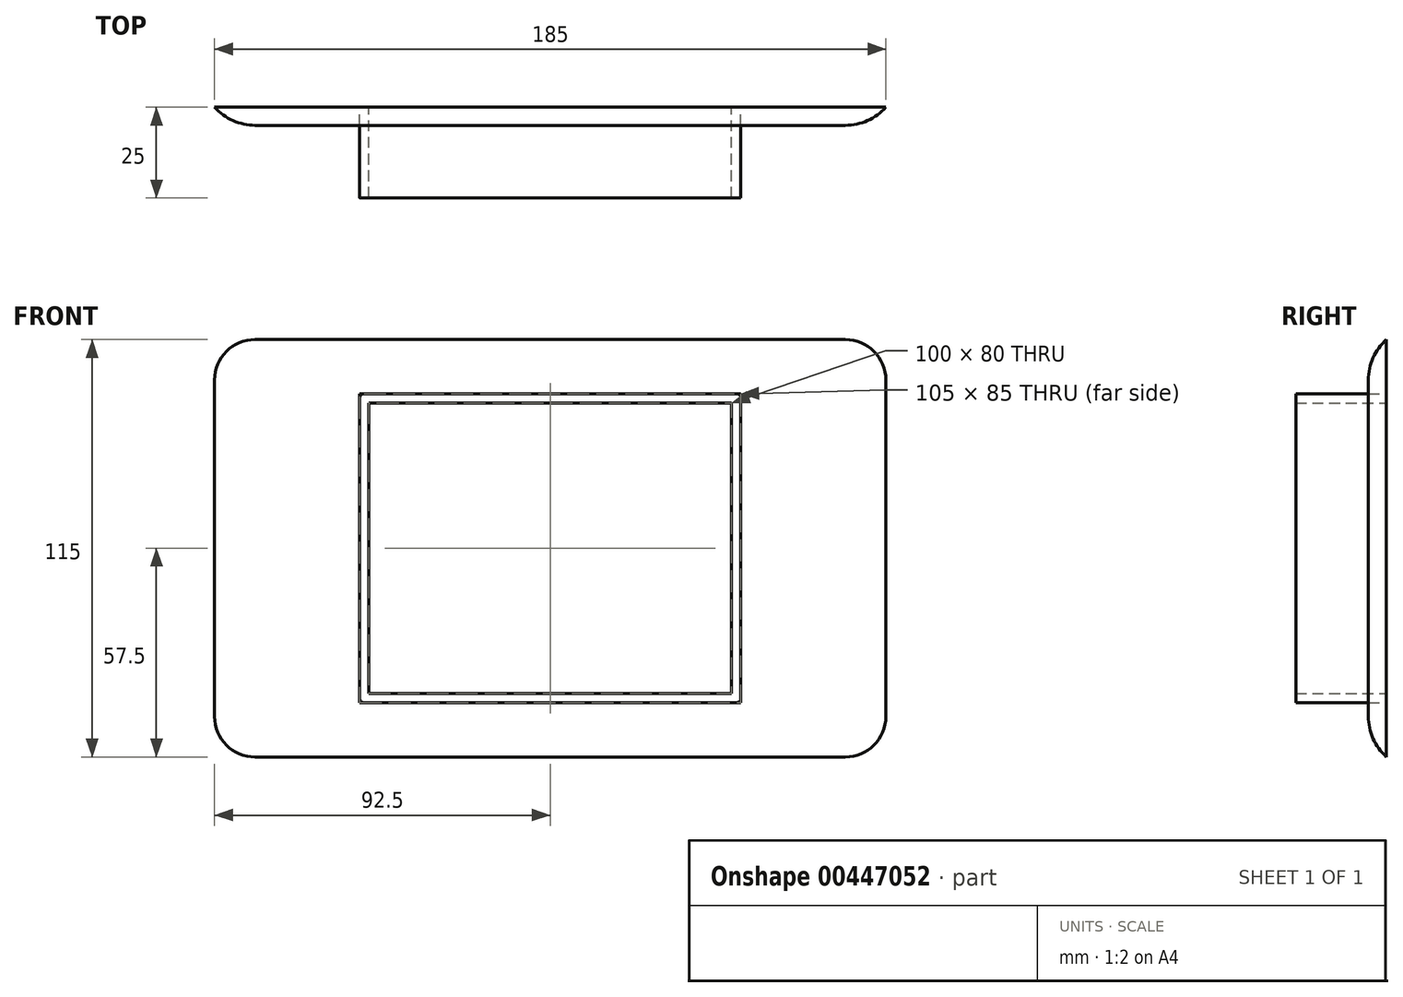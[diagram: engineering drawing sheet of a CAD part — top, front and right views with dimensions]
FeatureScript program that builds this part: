
annotation { "Feature Type Name" : "Feature", "Feature Type Description" : "" }
export const myFeature = defineFeature(function(context is Context, id is Id, definition is map)
    precondition{}
    {
        {
            var Q0;
            Q0=qCreatedBy(makeId("Front.planeOp"),FACE);
            var sketch = newSketch(context, id + "F0", { "sketchPlane" : qUnion([Q0])});
            skLineSegment(sketch, "E0.bottom", {"start": v(-92.5, 57.5) * mm, "end": v(92.5, 57.5) * mm});
            skLineSegment(sketch, "E0.top", {"start": v(-92.5, -57.5) * mm, "end": v(92.5, -57.5) * mm});
            skLineSegment(sketch, "E0.left", {"start": v(-92.5, 57.5) * mm, "end": v(-92.5, -57.5) * mm});
            skLineSegment(sketch, "E0.right", {"start": v(92.5, 57.5) * mm, "end": v(92.5, -57.5) * mm});
            skPoint(sketch, "E0.middle", {"position": v(0, 0) * mm});
            skLineSegment(sketch, "E1.bottom", {"start": v(-87.5, 52.5) * mm, "end": v(87.5, 52.5) * mm});
            skLineSegment(sketch, "E1.top", {"start": v(-87.5, -52.5) * mm, "end": v(87.5, -52.5) * mm});
            skLineSegment(sketch, "E1.left", {"start": v(-87.5, 52.5) * mm, "end": v(-87.5, -52.5) * mm});
            skLineSegment(sketch, "E1.right", {"start": v(87.5, 52.5) * mm, "end": v(87.5, -52.5) * mm});
            skLineSegment(sketch, "E2.bottom", {"start": v(-50, 40) * mm, "end": v(50, 40) * mm});
            skLineSegment(sketch, "E2.top", {"start": v(-50, -40) * mm, "end": v(50, -40) * mm});
            skLineSegment(sketch, "E2.left", {"start": v(-50, 40) * mm, "end": v(-50, -40) * mm});
            skLineSegment(sketch, "E2.right", {"start": v(50, 40) * mm, "end": v(50, -40) * mm});
            skLineSegment(sketch, "E3.bottom", {"start": v(-42.5, 30) * mm, "end": v(42.5, 30) * mm, "construction": true});
            skLineSegment(sketch, "E3.top", {"start": v(-42.5, -30) * mm, "end": v(42.5, -30) * mm, "construction": true});
            skLineSegment(sketch, "E3.left", {"start": v(-42.5, 30) * mm, "end": v(-42.5, -30) * mm, "construction": true});
            skLineSegment(sketch, "E3.right", {"start": v(42.5, 30) * mm, "end": v(42.5, -30) * mm, "construction": true});
            skCircle(sketch, "E4", {"center": v(-42.5, 30) * mm, "radius": 4 * mm});
            skCircle(sketch, "E5", {"center": v(42.5, 30) * mm, "radius": 4 * mm});
            skCircle(sketch, "E6", {"center": v(-42.5, -30) * mm, "radius": 4 * mm});
            skCircle(sketch, "E7", {"center": v(33.5, -31.5) * mm, "radius": 4 * mm});
            skCircle(sketch, "E8", {"center": v(-42.5, 30) * mm, "radius": 1.25 * mm});
            skCircle(sketch, "E9", {"center": v(42.5, 30) * mm, "radius": 1.25 * mm});
            skCircle(sketch, "E10", {"center": v(33.5, -31.5) * mm, "radius": 1.25 * mm});
            skCircle(sketch, "E11", {"center": v(-42.5, -30) * mm, "radius": 1.25 * mm});
            skLineSegment(sketch, "E12.bottom", {"start": v(-52.5, 42.5) * mm, "end": v(52.5, 42.5) * mm});
            skLineSegment(sketch, "E12.top", {"start": v(-52.5, -42.5) * mm, "end": v(52.5, -42.5) * mm});
            skLineSegment(sketch, "E12.left", {"start": v(-52.5, 42.5) * mm, "end": v(-52.5, -42.5) * mm});
            skLineSegment(sketch, "E12.right", {"start": v(52.5, 42.5) * mm, "end": v(52.5, -42.5) * mm});
            skSolve(sketch);
        }
        {
            var Q0;
            Q0=makeQuery(id+"F0.imprint","IMPRINT",FACE,{"disambiguationData":[TD([[makeQuery(id+"F0.imprint","IMPRINT",EDGE,{"derivedFrom":sQuery(id+"F0.wireOp",EDGE,"E0.bottom")}),-1.0]])]});
            var Q1;
            Q1=makeQuery(id+"F0.imprint","IMPRINT",FACE,{"disambiguationData":[TD([[makeQuery(id+"F0.imprint","IMPRINT",EDGE,{"derivedFrom":sQuery(id+"F0.wireOp",EDGE,"E1.bottom")}),-1.0]])]});
            extrude(context, id + "F1", {"entities" : qUnion([Q0, Q1]), "depth" : 5 * mm});
        }
        {
            var Q0;
            Q0=makeQuery(id+"F1.opExtrude","CAP_EDGE",EDGE,{"disambiguationData":[OSD([sQuery(id+"F0.wireOp",EDGE,"E0.left")])],"isStart":false});
            var Q1;
            Q1=makeQuery(id+"F1.opExtrude","CAP_EDGE",EDGE,{"disambiguationData":[OSD([sQuery(id+"F0.wireOp",EDGE,"E0.bottom")])],"isStart":false});
            var Q2;
            Q2=makeQuery(id+"F1.opExtrude","CAP_EDGE",EDGE,{"disambiguationData":[OSD([sQuery(id+"F0.wireOp",EDGE,"E0.top")])],"isStart":false});
            var Q3;
            Q3=makeQuery(id+"F1.opExtrude","CAP_EDGE",EDGE,{"disambiguationData":[OSD([sQuery(id+"F0.wireOp",EDGE,"E0.right")])],"isStart":false});
            fillet(context, id + "F2", {"entities" : qUnion([Q0, Q1, Q2, Q3]), "radius" : 15 * mm, "tangentPropagation" : true, "allowEdgeOverflow" : false});
        }
        {
            var Q0;
            Q0=makeQuery(id+"F2.opFillet","BLEND_EDGE",EDGE,{"blendedFrom":[makeQuery(id+"F1.opExtrude","CAP_EDGE",EDGE,{"disambiguationData":[OSD([sQuery(id+"F0.wireOp",EDGE,"E0.bottom")])],"isStart":false}),makeQuery(id+"F1.opExtrude","CAP_EDGE",EDGE,{"disambiguationData":[OSD([sQuery(id+"F0.wireOp",EDGE,"E0.left")])],"isStart":false})],"blendedInto":[]});
            var Q1;
            Q1=makeQuery(id+"F2.opFillet","BLEND_EDGE",EDGE,{"blendedFrom":[makeQuery(id+"F1.opExtrude","CAP_EDGE",EDGE,{"disambiguationData":[OSD([sQuery(id+"F0.wireOp",EDGE,"E0.top")])],"isStart":false}),makeQuery(id+"F1.opExtrude","CAP_EDGE",EDGE,{"disambiguationData":[OSD([sQuery(id+"F0.wireOp",EDGE,"E0.left")])],"isStart":false})],"blendedInto":[]});
            var Q2;
            Q2=makeQuery(id+"F2.opFillet","BLEND_EDGE",EDGE,{"blendedFrom":[makeQuery(id+"F1.opExtrude","CAP_EDGE",EDGE,{"disambiguationData":[OSD([sQuery(id+"F0.wireOp",EDGE,"E0.top")])],"isStart":false}),makeQuery(id+"F1.opExtrude","CAP_EDGE",EDGE,{"disambiguationData":[OSD([sQuery(id+"F0.wireOp",EDGE,"E0.right")])],"isStart":false})],"blendedInto":[]});
            var Q3;
            Q3=makeQuery(id+"F2.opFillet","BLEND_EDGE",EDGE,{"blendedFrom":[makeQuery(id+"F1.opExtrude","CAP_EDGE",EDGE,{"disambiguationData":[OSD([sQuery(id+"F0.wireOp",EDGE,"E0.bottom")])],"isStart":false}),makeQuery(id+"F1.opExtrude","CAP_EDGE",EDGE,{"disambiguationData":[OSD([sQuery(id+"F0.wireOp",EDGE,"E0.right")])],"isStart":false})],"blendedInto":[]});
            fillet(context, id + "F3", {"entities" : qUnion([Q0, Q1, Q2, Q3]), "radius" : 15 * mm, "tangentPropagation" : true, "allowEdgeOverflow" : false});
        }
        {
            var Q0;
            Q0=makeQuery(id+"F0.imprint","IMPRINT",FACE,{"disambiguationData":[TD([[makeQuery(id+"F0.imprint","IMPRINT",EDGE,{"derivedFrom":sQuery(id+"F0.wireOp",EDGE,"E2.bottom")}),1.0]])]});
            extrude(context, id + "F4", {"entities" : qUnion([Q0]), "depth" : 25 * mm});
        }
        {
            var Q0;
            Q0=makeQuery(id+"F4.opExtrude","SWEPT_EDGE",EDGE,{"disambiguationData":[OSD([sQuery(id+"F0.wireOp",EDGE,"E12.bottom"),sQuery(id+"F0.wireOp",EDGE,"E12.left")])]});
            var Q1;
            Q1=makeQuery(id+"F4.opExtrude","SWEPT_EDGE",EDGE,{"disambiguationData":[OSD([sQuery(id+"F0.wireOp",EDGE,"E12.top"),sQuery(id+"F0.wireOp",EDGE,"E12.left")])]});
            var Q2;
            Q2=makeQuery(id+"F4.opExtrude","SWEPT_EDGE",EDGE,{"disambiguationData":[OSD([sQuery(id+"F0.wireOp",EDGE,"E12.bottom"),sQuery(id+"F0.wireOp",EDGE,"E12.right")])]});
            var Q3;
            Q3=makeQuery(id+"F4.opExtrude","SWEPT_EDGE",EDGE,{"disambiguationData":[OSD([sQuery(id+"F0.wireOp",EDGE,"E12.top"),sQuery(id+"F0.wireOp",EDGE,"E12.right")])]});
            fillet(context, id + "F5", {"entities" : qUnion([Q0, Q1, Q2, Q3]), "radius" : 1 * mm, "tangentPropagation" : true, "allowEdgeOverflow" : false});
        }
    });
